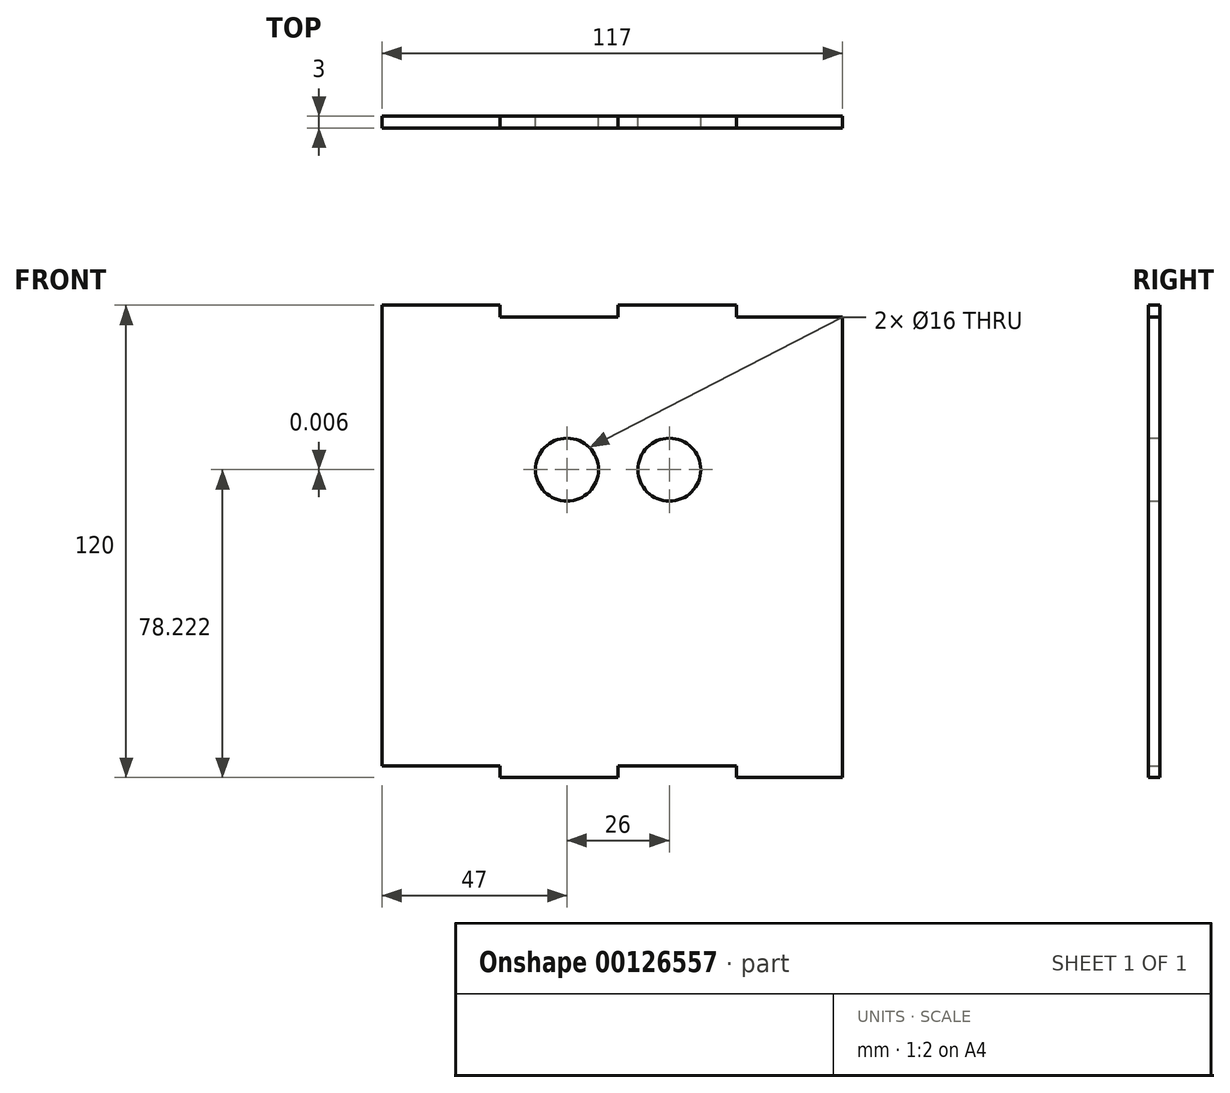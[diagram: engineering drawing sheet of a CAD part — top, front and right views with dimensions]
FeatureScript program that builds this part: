
annotation { "Feature Type Name" : "Feature", "Feature Type Description" : "" }
export const myFeature = defineFeature(function(context is Context, id is Id, definition is map)
    precondition{}
    {
        {
            var Q0;
            Q0=qCreatedBy(makeId("Front.planeOp"),FACE);
            var sketch = newSketch(context, id + "F0", { "sketchPlane" : qUnion([Q0])});
            skLineSegment(sketch, "E0", {"start": v(0, 0) * mm, "end": v(0, 0) * mm});
            skPoint(sketch, "E1.middle", {"position": v(0, 75.23) * mm});
            skCircle(sketch, "E2", {"center": v(-13, 75.23) * mm, "radius": 8 * mm});
            skCircle(sketch, "E3.MirrorC", {"center": v(13, 75.22) * mm, "radius": 8 * mm});
            skLineSegment(sketch, "E4", {"start": v(0, 75.23) * mm, "end": v(0, 0) * mm, "construction": true});
            skLineSegment(sketch, "E5", {"start": v(-21, 74.98) * mm, "end": v(21, 75.22) * mm, "construction": true});
            skLineSegment(sketch, "E6", {"start": v(-5, 75.07) * mm, "end": v(5, 75.13) * mm, "construction": true});
            skLineSegment(sketch, "E7", {"start": v(0, 75.23) * mm, "end": v(0, 100) * mm, "construction": true});
            skLineSegment(sketch, "E8", {"start": v(0, 100) * mm, "end": v(0, -3) * mm, "construction": true});
            skLineSegment(sketch, "E9", {"start": v(0, -3) * mm, "end": v(-30, -3) * mm});
            skLineSegment(sketch, "E10", {"start": v(30, -3) * mm, "end": v(57, -3) * mm});
            skLineSegment(sketch, "E11", {"start": v(-60, 0) * mm, "end": v(-30, 0) * mm});
            skLineSegment(sketch, "E12", {"start": v(-30, 0) * mm, "end": v(-30, -3) * mm});
            skLineSegment(sketch, "E13", {"start": v(-30, -3) * mm, "end": v(0, -3) * mm});
            skLineSegment(sketch, "E14", {"start": v(0, -3) * mm, "end": v(0, 0) * mm});
            skLineSegment(sketch, "E15", {"start": v(0, 0) * mm, "end": v(30, 0) * mm});
            skLineSegment(sketch, "E16", {"start": v(30, 0) * mm, "end": v(30, -3) * mm});
            skLineSegment(sketch, "E17", {"start": v(57, -3) * mm, "end": v(57, 114) * mm});
            skLineSegment(sketch, "E18", {"start": v(30, 117) * mm, "end": v(0, 117) * mm});
            skLineSegment(sketch, "E19", {"start": v(-60, 117) * mm, "end": v(-60, 0) * mm});
            skLineSegment(sketch, "E20", {"start": v(-60, 117) * mm, "end": v(-30, 117) * mm});
            skLineSegment(sketch, "E21", {"start": v(-30, 117) * mm, "end": v(-30, 114) * mm});
            skLineSegment(sketch, "E22", {"start": v(-30, 114) * mm, "end": v(0, 114) * mm});
            skLineSegment(sketch, "E23", {"start": v(0, 114) * mm, "end": v(0, 117) * mm});
            skLineSegment(sketch, "E24", {"start": v(0, 117) * mm, "end": v(30, 117) * mm});
            skLineSegment(sketch, "E25", {"start": v(30, 117) * mm, "end": v(30, 114) * mm});
            skLineSegment(sketch, "E26", {"start": v(30, 114) * mm, "end": v(57, 114) * mm});
            skLineSegment(sketch, "E27.trimOffspring", {"start": v(-30, 117) * mm, "end": v(-60, 117) * mm});
            skSolve(sketch);
        }
        {
            var Q0;
            Q0=makeQuery(id+"F0.imprint","IMPRINT",FACE,{"disambiguationData":[TD([[makeQuery(id+"F0.imprint","IMPRINT",EDGE,{"derivedFrom":sQuery(id+"F0.wireOp",EDGE,"59JATPGQ-tOle-Dk2i-3esh-BRPMtyhtL81G.bottom")}),1.0]])]});
            var Q1;
            Q1=makeQuery(id+"F0.imprint","IMPRINT",FACE,{"disambiguationData":[TD([[makeQuery(id+"F0.imprint","IMPRINT",EDGE,{"derivedFrom":sQuery(id+"F0.wireOp",EDGE,"E2")}),-1.0]])]});
            extrude(context, id + "F1", {"entities" : qUnion([Q0, Q1]), "endBound" : BoundingType.SYMMETRIC, "depth" : 3 * mm});
        }
    });
